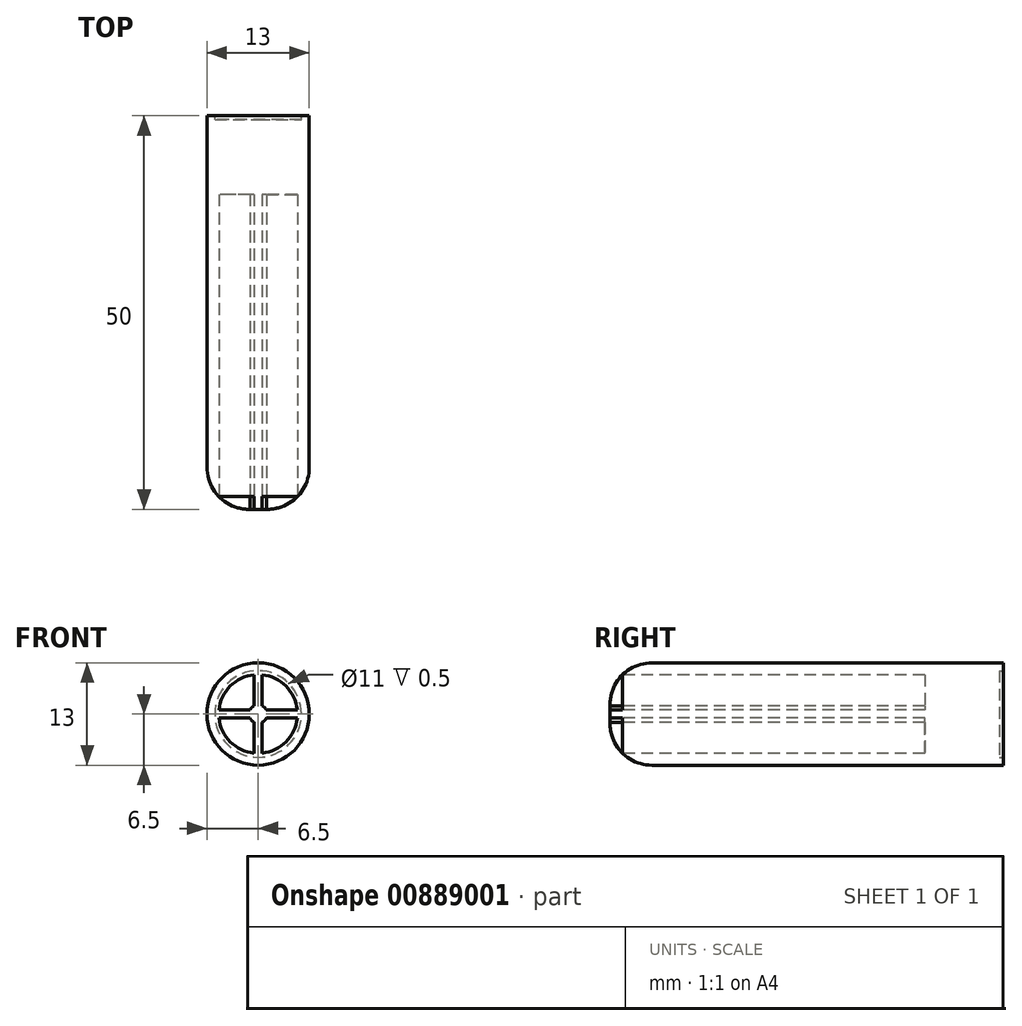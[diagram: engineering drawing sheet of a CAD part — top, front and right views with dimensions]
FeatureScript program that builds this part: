
annotation { "Feature Type Name" : "Feature", "Feature Type Description" : "" }
export const myFeature = defineFeature(function(context is Context, id is Id, definition is map)
    precondition{}
    {
        {
            var Q0;
            Q0=qCreatedBy(makeId("Front.planeOp"),FACE);
            var sketch = newSketch(context, id + "F0", { "sketchPlane" : qUnion([Q0])});
            skCircle(sketch, "E0", {"center": v(0, 0) * mm, "radius": 6.5 * mm});
            skSolve(sketch);
        }
        {
            var Q0;
            Q0 = qSketchRegion(id + "F0", true);
            var Q1;
            Q1=makeQuery(id+"F0.imprint","IMPRINT",FACE,{"disambiguationData":[TD([[makeQuery(id+"F0.imprint","IMPRINT",EDGE,{"derivedFrom":sQuery(id+"F0.wireOp",EDGE,"E0")}),1.0]])]});
            extrude(context, id + "F1", {"entities" : qUnion([Q0, Q1]), "depth" : 50 * mm, "offsetDistance" : 25.4 * mm});
        }
        {
            var Q0;
            Q0=makeQuery(id+"F1.opExtrude","CAP_EDGE",EDGE,{"disambiguationData":[OSD([sQuery(id+"F0.wireOp",EDGE,"E0")])],"isStart":false});
            fillet(context, id + "F2", {"entities" : qUnion([Q0]), "radius" : 5.33 * mm, "tangentPropagation" : true, "allowEdgeOverflow" : false});
        }
        {
            var Q0;
            Q0=makeQuery(id+"F1.opExtrude","CAP_FACE",FACE,{"disambiguationData":[OSD([sQuery(id+"F0.wireOp",EDGE,"E0")])],"isStart":false});
            var sketch = newSketch(context, id + "F3", { "sketchPlane" : qUnion([Q0])});
            skCircle(sketch, "E1", {"center": v(0, 0) * mm, "radius": 5 * mm});
            skLineSegment(sketch, "E2", {"start": v(-0.5, 4.97) * mm, "end": v(-0.5, 0.5) * mm});
            skLineSegment(sketch, "E3", {"start": v(-0.5, 0.5) * mm, "end": v(-4.97, 0.5) * mm});
            skLineSegment(sketch, "E4", {"start": v(0.5, 4.97) * mm, "end": v(0.5, 0.5) * mm});
            skLineSegment(sketch, "E5", {"start": v(0.5, 0.5) * mm, "end": v(4.97, 0.5) * mm});
            skLineSegment(sketch, "E6", {"start": v(-4.97, -0.5) * mm, "end": v(-0.5, -0.5) * mm});
            skLineSegment(sketch, "E7", {"start": v(-0.5, -0.5) * mm, "end": v(-0.5, -4.97) * mm});
            skLineSegment(sketch, "E8", {"start": v(4.97, -0.5) * mm, "end": v(0.5, -0.5) * mm});
            skLineSegment(sketch, "E9", {"start": v(0.5, -0.5) * mm, "end": v(0.5, -4.97) * mm});
            skSolve(sketch);
        }
        {
            var Q0;
            {var subQ0=sQuery(id+"F3.wireOp",EDGE,"E2");var subQ1=sQuery(id+"F3.wireOp",EDGE,"E1");var subQ2=makeQuery(id+"F3.imprint","INTERSECT",VERTEX,{"derivedFrom":[subQ1,subQ0]});Q0=makeQuery(id+"F3.imprint","IMPRINT",FACE,{"disambiguationData":[TD([[makeQuery(id+"F3.imprint","IMPRINT",EDGE,{"disambiguationData":[TD([[subQ2,-1.0]])],"derivedFrom":subQ1}),1.0]])]});}
            var Q1;
            {var subQ0=sQuery(id+"F3.wireOp",EDGE,"E4");var subQ1=sQuery(id+"F3.wireOp",EDGE,"E1");var subQ2=makeQuery(id+"F3.imprint","INTERSECT",VERTEX,{"derivedFrom":[subQ1,subQ0]});Q1=makeQuery(id+"F3.imprint","IMPRINT",FACE,{"disambiguationData":[TD([[makeQuery(id+"F3.imprint","IMPRINT",EDGE,{"disambiguationData":[TD([[subQ2,1.0]])],"derivedFrom":subQ1}),1.0]])]});}
            var Q2;
            {var subQ0=sQuery(id+"F3.wireOp",EDGE,"E8");var subQ1=sQuery(id+"F3.wireOp",EDGE,"E1");var subQ2=makeQuery(id+"F3.imprint","INTERSECT",VERTEX,{"derivedFrom":[subQ1,subQ0]});Q2=makeQuery(id+"F3.imprint","IMPRINT",FACE,{"disambiguationData":[TD([[makeQuery(id+"F3.imprint","IMPRINT",EDGE,{"disambiguationData":[TD([[subQ2,1.0]])],"derivedFrom":subQ1}),1.0]])]});}
            var Q3;
            {var subQ0=sQuery(id+"F3.wireOp",EDGE,"E6");var subQ1=sQuery(id+"F3.wireOp",EDGE,"E1");var subQ2=makeQuery(id+"F3.imprint","INTERSECT",VERTEX,{"derivedFrom":[subQ1,subQ0]});Q3=makeQuery(id+"F3.imprint","IMPRINT",FACE,{"disambiguationData":[TD([[makeQuery(id+"F3.imprint","IMPRINT",EDGE,{"disambiguationData":[TD([[subQ2,-1.0]])],"derivedFrom":subQ1}),1.0]])]});}
            extrude(context, id + "F4", {"entities" : qUnion([Q0, Q1, Q2, Q3]), "operationType" : NewBodyOperationType.REMOVE, "oppositeDirection" : true, "depth" : 40 * mm, "offsetDistance" : 25.4 * mm});
        }
        {
            var Q0;
            Q0=makeQuery(id+"F1.opExtrude","CAP_FACE",FACE,{"disambiguationData":[OSD([sQuery(id+"F0.wireOp",EDGE,"E0")])],"isStart":true});
            var sketch = newSketch(context, id + "F5", { "sketchPlane" : qUnion([Q0])});
            skCircle(sketch, "E10", {"center": v(0, 0) * mm, "radius": 5.5 * mm});
            skSolve(sketch);
        }
        {
            var Q0;
            Q0=makeQuery(id+"F5.imprint","IMPRINT",FACE,{"disambiguationData":[TD([[makeQuery(id+"F5.imprint","IMPRINT",EDGE,{"derivedFrom":sQuery(id+"F5.wireOp",EDGE,"E10")}),1.0]])]});
            extrude(context, id + "F6", {"entities" : qUnion([Q0]), "operationType" : NewBodyOperationType.REMOVE, "oppositeDirection" : true, "depth" : .5 * mm, "offsetDistance" : 25.4 * mm});
        }
    });
